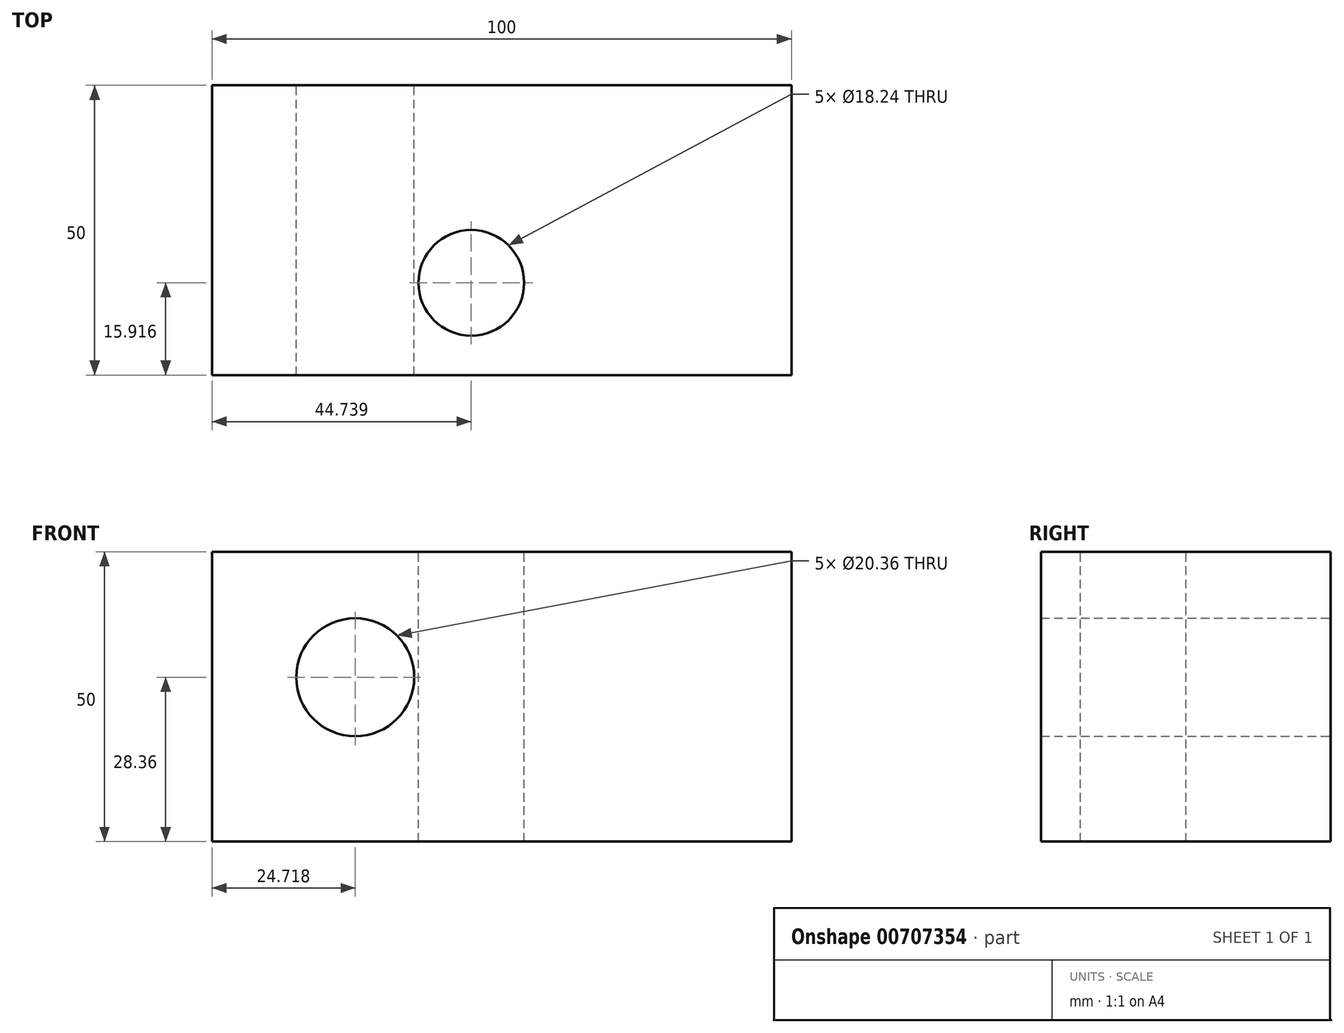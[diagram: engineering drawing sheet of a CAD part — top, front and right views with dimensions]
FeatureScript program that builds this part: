
annotation { "Feature Type Name" : "Feature", "Feature Type Description" : "" }
export const myFeature = defineFeature(function(context is Context, id is Id, definition is map)
    precondition{}
    {
        {
            var Q0;
            Q0=qCreatedBy(makeId("Top.planeOp"),FACE);
            var sketch = newSketch(context, id + "F0", { "sketchPlane" : qUnion([Q0])});
            skLineSegment(sketch, "E0.bottom", {"start": v(-52.81, 18.7) * mm, "end": v(47.19, 18.7) * mm});
            skLineSegment(sketch, "E0.top", {"start": v(-52.81, -31.3) * mm, "end": v(47.19, -31.3) * mm});
            skLineSegment(sketch, "E0.left", {"start": v(-52.81, 18.7) * mm, "end": v(-52.81, -31.3) * mm});
            skLineSegment(sketch, "E0.right", {"start": v(47.19, 18.7) * mm, "end": v(47.19, -31.3) * mm});
            skSolve(sketch);
        }
        {
            var Q0;
            Q0=makeQuery(id+"F0.imprint","IMPRINT",FACE,{"disambiguationData":[TD([[makeQuery(id+"F0.imprint","IMPRINT",EDGE,{"derivedFrom":sQuery(id+"F0.wireOp",EDGE,"E0.bottom")}),-1.0]])]});
            extrude(context, id + "F1", {"entities" : qUnion([Q0]), "depth" : 50 * mm, "offsetDistance" : 25 * mm});
        }
        {
            var Q0;
            Q0=makeQuery(id+"F1.opExtrude","CAP_FACE",FACE,{"disambiguationData":[OSD([sQuery(id+"F0.wireOp",EDGE,"E0.bottom"),sQuery(id+"F0.wireOp",EDGE,"E0.top"),sQuery(id+"F0.wireOp",EDGE,"E0.left"),sQuery(id+"F0.wireOp",EDGE,"E0.right")])],"isStart":false});
            var sketch = newSketch(context, id + "F2", { "sketchPlane" : qUnion([Q0])});
            skCircle(sketch, "E1", {"center": v(-8.07, -15.38) * mm, "radius": 9.12 * mm});
            skSolve(sketch);
        }
        {
            var Q0;
            Q0=makeQuery(id+"F2.imprint","IMPRINT",FACE,{"disambiguationData":[TD([[makeQuery(id+"F2.imprint","IMPRINT",EDGE,{"derivedFrom":sQuery(id+"F2.wireOp",EDGE,"E1")}),1.0]])]});
            extrude(context, id + "F3", {"entities" : qUnion([Q0]), "operationType" : NewBodyOperationType.REMOVE, "endBound" : BoundingType.UP_TO_NEXT, "oppositeDirection" : true, "depth" : 25 * mm, "offsetDistance" : 25 * mm});
        }
        {
            var Q0;
            Q0=makeQuery(id+"F1.opExtrude","SWEPT_FACE",FACE,{"disambiguationData":[OSD([sQuery(id+"F0.wireOp",EDGE,"E0.bottom")])]});
            var sketch = newSketch(context, id + "F4", { "sketchPlane" : qUnion([Q0])});
            skCircle(sketch, "E2", {"center": v(28.1, 28.36) * mm, "radius": 10.18 * mm});
            skSolve(sketch);
        }
        {
            var Q0;
            Q0=makeQuery(id+"F4.imprint","IMPRINT",FACE,{"disambiguationData":[TD([[makeQuery(id+"F4.imprint","IMPRINT",EDGE,{"derivedFrom":sQuery(id+"F4.wireOp",EDGE,"E2")}),1.0]])]});
            extrude(context, id + "F5", {"entities" : qUnion([Q0]), "operationType" : NewBodyOperationType.REMOVE, "endBound" : BoundingType.UP_TO_NEXT, "oppositeDirection" : true, "depth" : 25 * mm, "offsetDistance" : 25 * mm});
        }
    });
